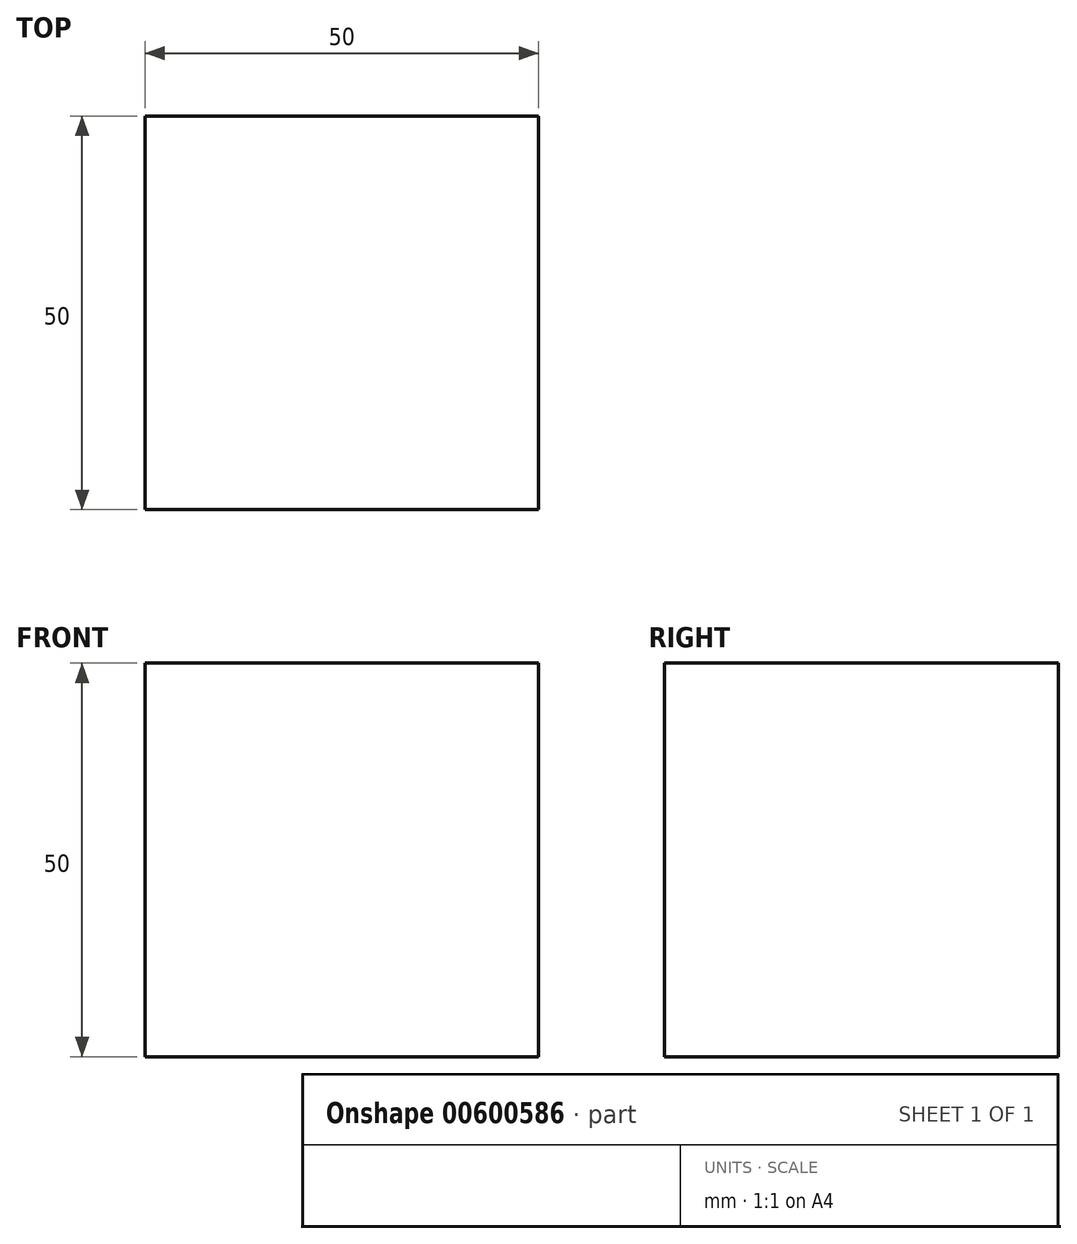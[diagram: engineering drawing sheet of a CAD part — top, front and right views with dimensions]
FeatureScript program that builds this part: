
annotation { "Feature Type Name" : "Feature", "Feature Type Description" : "" }
export const myFeature = defineFeature(function(context is Context, id is Id, definition is map)
    precondition{}
    {
        {
            var Q0;
            Q0=qCreatedBy(makeId("Top.planeOp"),FACE);
            var sketch = newSketch(context, id + "F0", { "sketchPlane" : qUnion([Q0])});
            skLineSegment(sketch, "E0.bottom", {"start": v(12.29, -24.7) * mm, "end": v(-37.71, -24.7) * mm});
            skLineSegment(sketch, "E0.top", {"start": v(12.29, 25.3) * mm, "end": v(-37.71, 25.3) * mm});
            skLineSegment(sketch, "E0.left", {"start": v(12.29, -24.7) * mm, "end": v(12.29, 25.3) * mm});
            skLineSegment(sketch, "E0.right", {"start": v(-37.71, -24.7) * mm, "end": v(-37.71, 25.3) * mm});
            skSolve(sketch);
        }
        {
            var Q0;
            Q0 = qSketchRegion(id + "F0", true);
            extrude(context, id + "F1", {"entities" : qUnion([Q0]), "depth" : 50 * mm, "offsetDistance" : 25 * mm});
        }
    });
